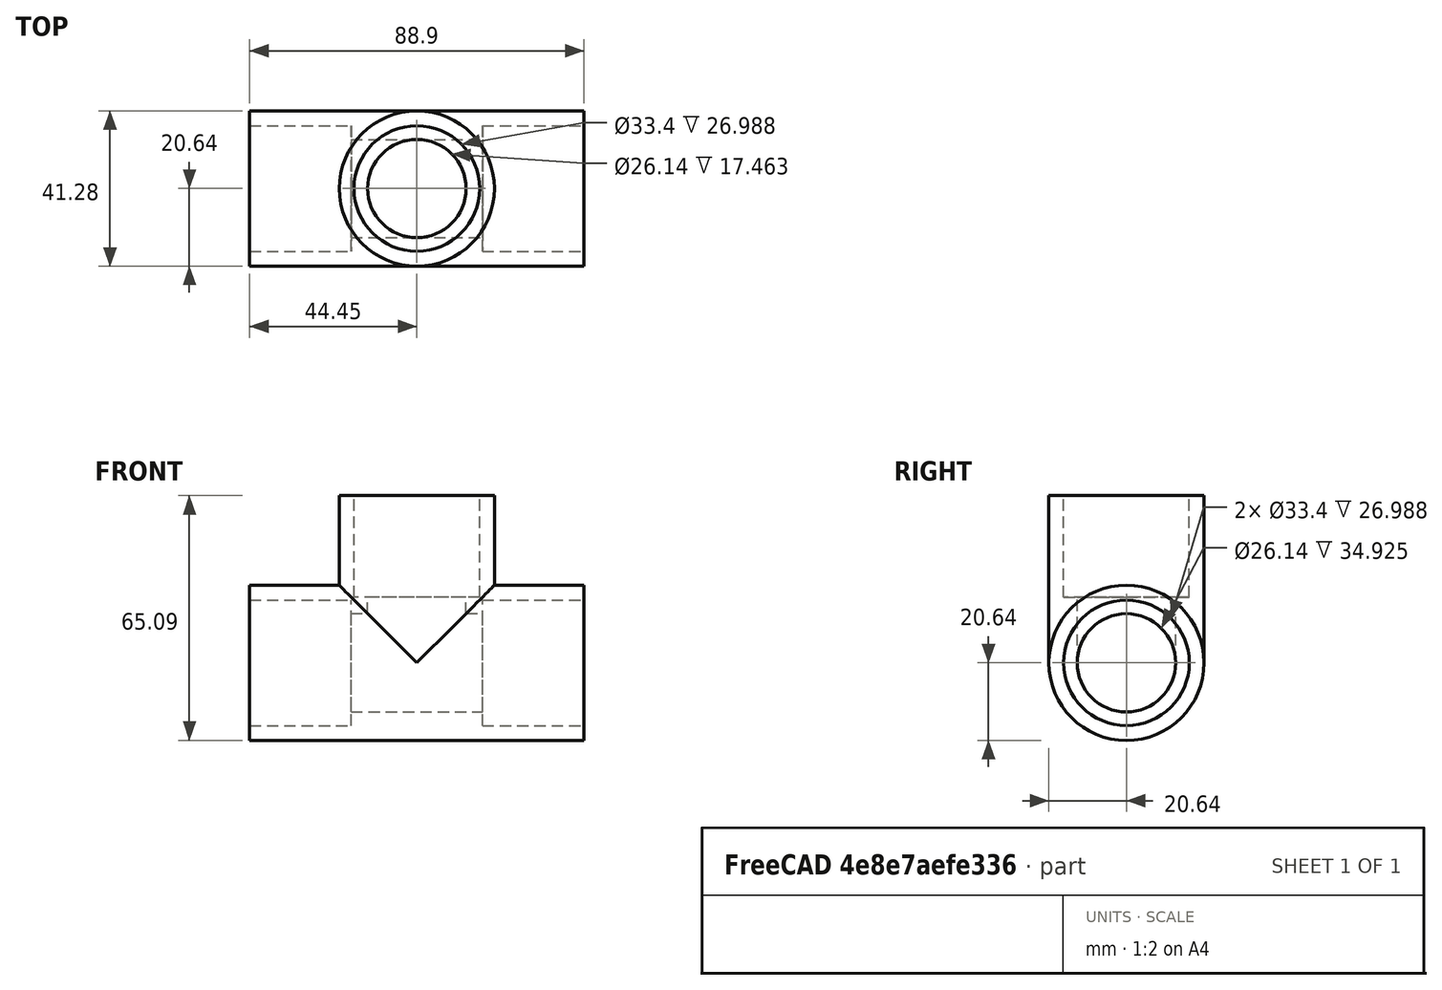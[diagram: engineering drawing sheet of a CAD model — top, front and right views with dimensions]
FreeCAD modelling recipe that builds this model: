
FCSTD DOCUMENT  (FreeCAD 0.17R13303 (Git))
Label: tee-test
License: All rights reserved
LicenseURL: http://en.wikipedia.org/wiki/All_rights_reserved
objects: Part::Cylinder×7, Part::MultiFuse×3, Part::Cut×2
note: 12 computed .brp shape members not serialized (recipe doc carries the construction recipe); baked Part::Feature solids carry a one-line shape summary decoded from their .brp

FEATURE [Part::Cylinder] VerticalOuterCynlider
  Angle = 360
  AttacherType = Attacher::AttachEngine3D
  Height = 44.45
  Radius = 20.6375
FEATURE [Part::Cylinder] VerticalInnerCynlider
  Angle = 360
  AttacherType = Attacher::AttachEngine3D
  Height = 48.895
  Radius = 13.0683
FEATURE [Part::Cylinder] HorizontalOuterCynlider
  Angle = 360
  AttacherType = Attacher::AttachEngine3D
  Height = 88.9
  Placement = pos=(-44.45,0,0) rot=(0,1,0;1.5708rad)
  Radius = 20.6375
FEATURE [Part::Cylinder] HorizontalInnerCynlider
  Angle = 360
  AttacherType = Attacher::AttachEngine3D
  Height = 97.79
  Placement = pos=(-48.895,0,0) rot=(0,1,0;1.5708rad)
  Radius = 13.0683
FEATURE [Part::MultiFuse] OuterTeeFusion
  Shapes = -> [VerticalOuterCynlider,HorizontalOuterCynlider]
FEATURE [Part::MultiFuse] InnerTeeFusion
  Shapes = -> [VerticalInnerCynlider,HorizontalInnerCynlider]
FEATURE [Part::Cut] Cut
  Base = -> OuterTeeFusion
  Tool = -> InnerTeeFusion
FEATURE [Part::Cylinder] SocketLeft
  Angle = 360
  AttacherType = Attacher::AttachEngine3D
  Height = 29.6863
  Placement = pos=(-47.1487,0,0) rot=(0,1,0;1.5708rad)
  Radius = 16.7005
FEATURE [Part::Cylinder] SocketRight
  Angle = 360
  AttacherType = Attacher::AttachEngine3D
  Height = 29.6863
  Placement = pos=(17.4625,0,0) rot=(0,1,0;1.5708rad)
  Radius = 16.7005
FEATURE [Part::Cylinder] SocketTop
  Angle = 360
  AttacherType = Attacher::AttachEngine3D
  Height = 29.6863
  Placement = pos=(0,0,17.4625) rot=(0,1,0;0rad)
  Radius = 16.7005
FEATURE [Part::MultiFuse] Sockets
  Shapes = -> [SocketLeft,SocketRight,SocketTop]
FEATURE [Part::Cut] Tee  label="401-010"
  Base = -> Cut
  Tool = -> Sockets
